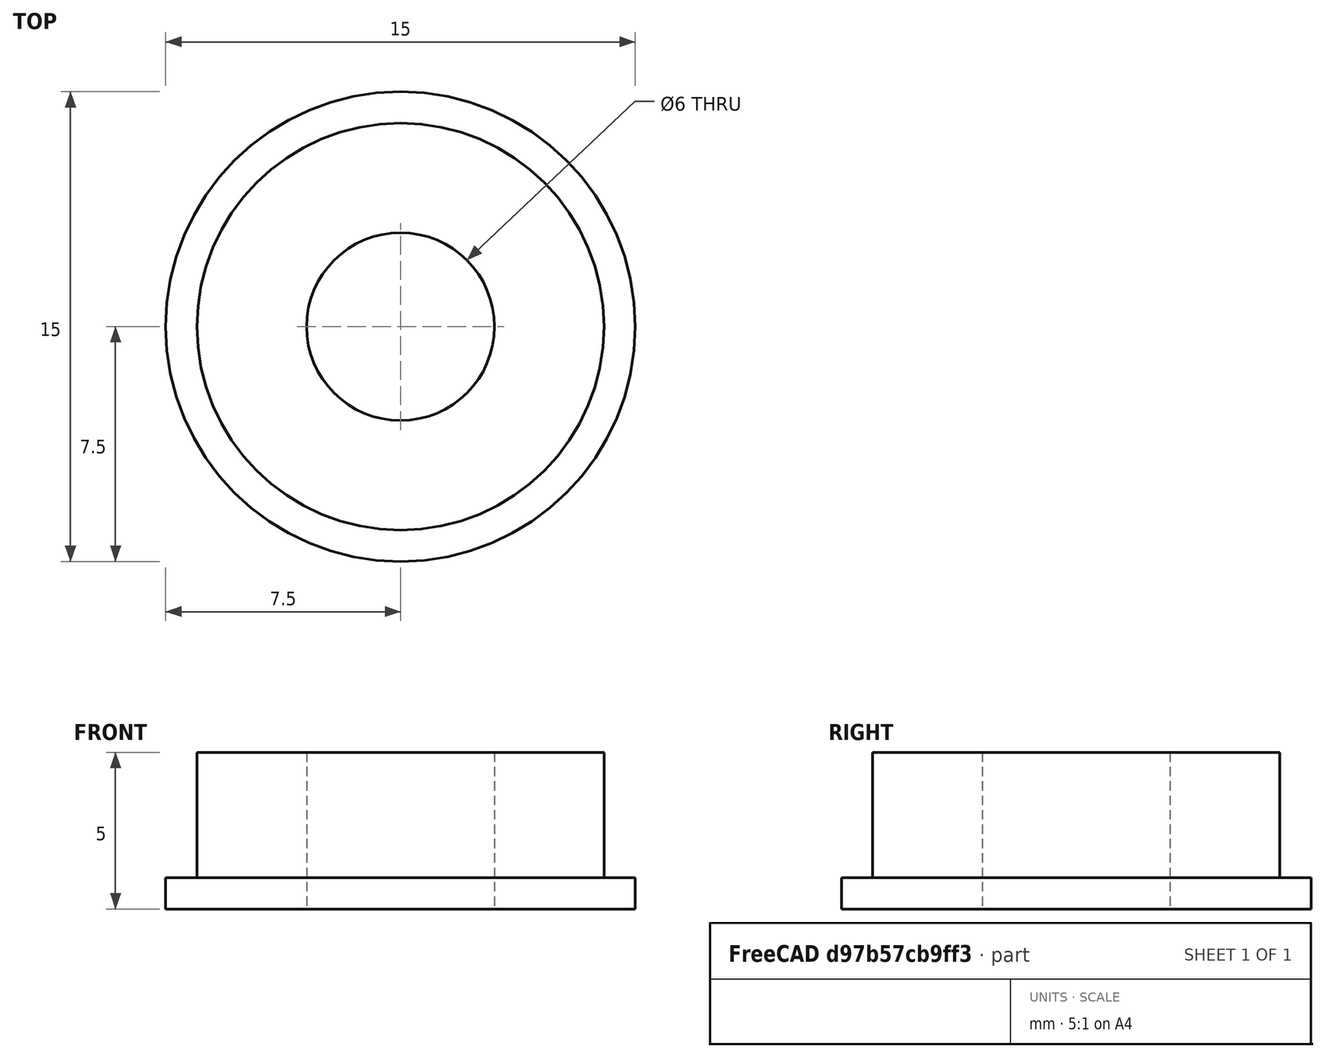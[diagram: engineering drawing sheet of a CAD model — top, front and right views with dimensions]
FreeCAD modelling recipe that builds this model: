
FCSTD DOCUMENT  (FreeCAD 1.0R39319 (Git))
Label: Bearing
License: All rights reserved
LicenseURL: https://en.wikipedia.org/wiki/All_rights_reserved
objects: Sketcher::SketchObject×1, PartDesign::Revolution×1, PartDesign::Body×1
note: 6 computed .brp shape members not serialized (recipe doc carries the construction recipe); baked Part::Feature solids carry a one-line shape summary decoded from their .brp

FEATURE [Sketcher::SketchObject] Sketch
  ArcFitTolerance = 1e-06
  AttachmentSupport = -> [XZ_Plane]
  FullyConstrained = true
  MakeInternals = false
  MapMode = 5
  Placement = pos=(0,0,0) rot=(1,0,0;1.5708rad)
  sketch-geometry (6):
    g0: LineSegment StartX=-3 StartY=0 StartZ=0 EndX=-7.5 EndY=0 EndZ=0
    g1: LineSegment StartX=-7.5 StartY=0 StartZ=0 EndX=-7.5 EndY=1 EndZ=0
    g2: LineSegment StartX=-7.5 StartY=1 StartZ=0 EndX=-6.5 EndY=1 EndZ=0
    g3: LineSegment StartX=-6.5 StartY=1 StartZ=0 EndX=-6.5 EndY=5 EndZ=0
    g4: LineSegment StartX=-6.5 StartY=5 StartZ=0 EndX=-3 EndY=5 EndZ=0
    g5: LineSegment StartX=-3 StartY=5 StartZ=0 EndX=-3 EndY=0 EndZ=0
  constraints (18):
    c: PointOnObject(g0,g-1)
    c: PointOnObject(g0,g-1)
    c: Coincident(g0,g1)
    c: Vertical(g1)
    c: Coincident(g1,g2)
    c: Horizontal(g2)
    c: Coincident(g2,g3)
    c: Vertical(g3)
    c: Coincident(g3,g4)
    c: Horizontal(g4)
    c: Coincident(g4,g5)
    c: Coincident(g5,g0)
    c: Vertical(g5)
    c: DistanceX(g0,g-1) = 7.5
    c: Distance(g-2,g5) = 3
    c: DistanceY(g1,g1) = 1
    c: Distance(g-2,g3) = 6.5
    c: Distance(g-1,g4) = 5
FEATURE [PartDesign::Revolution] Revolution
  Angle = 360
  Angle2 = 60
  Axis = (0,2e-16,1)
  Base = (0,0,0)
  Placement = pos=(0,0,0) rot=(1,0,0;1.5708rad)
  Profile = -> Sketch
  ReferenceAxis = -> Sketch [V_Axis]
  Refine = true
  Suppressed = false
  Type = 0
FEATURE [PartDesign::Body] Body  label="F686zz"
  AllowCompound = false
  Group = -> [Sketch,Revolution]
  Origin = -> Origin
  Tip = -> Revolution
